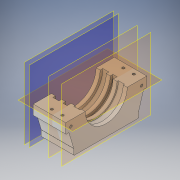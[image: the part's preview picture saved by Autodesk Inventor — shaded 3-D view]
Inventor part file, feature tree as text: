
AUTODESK INVENTOR PART (.ipt)
format: ipt  version: 2019 (Build 230136000, 136)  size: 584,192 bytes
history: native  units: mm
features: sketch x27, extrude x22, mirror x13, projected_geometry x13, plane x12, other x4, fillet x4, hole x3
ambient origin geometry x8: Origin, YZ Plane, XZ Plane, XY Plane, X Axis, Y Axis, Z Axis, Center Point
bodies: Body1 (feature_tree)
feature tree (98):
  other  "實體1"
  extrude  "擠出1"  Depth=123.43mm
  plane  "工作平面2"
  extrude  "擠出3"  Depth=160.0mm
  plane  "工作平面3"
  extrude  "擠出4"  Depth=120.0mm TaperAngle=0.0deg
  extrude  "擠出5"  [1 undecoded]
  plane  "工作平面4"
  extrude  "擠出7"  Depth=130.0mm
  plane  "工作平面5"
  extrude  "擠出9"  Depth=15.0mm TaperAngle=0.0deg
  extrude  "擠出10"  [1 undecoded]
  extrude  "擠出11"  Depth=111.375mm
  extrude  "擠出12"  Depth=10.0mm TaperAngle=0.0deg
  mirror  "鏡射1"
  fillet  "圓角2"  Radius=10.0mm
  fillet  "圓角3"  Radius=10.0mm
  sketch  "草圖16"
  plane  "工作平面7"
  mirror  "鏡射2"
  fillet  "圓角5"  [1 undecoded]
  fillet  "圓角6"  Radius=10.0mm
  plane  "工作平面8"
  plane  "工作平面9"
  sketch  "草圖20"
  extrude  "擠出15"  [1 undecoded]
  plane  "工作平面10"
  extrude  "擠出16"  Depth=10.0mm
  extrude  "擠出17"  Depth=10.0mm TaperAngle=0.0deg
  plane  "工作平面11"
  extrude  "擠出19"  Depth=10.0mm TaperAngle=0.0deg
  extrude  "擠出20"  Depth=160.0mm
  mirror  "鏡射3"
  mirror  "鏡射4"
  extrude  "擠出21"  Depth=80.0mm
  mirror  "鏡射7"
  plane  "工作平面15"
  mirror  "鏡射9"
  hole  "孔2"  [1 undecoded]
  mirror  "鏡射10"
  mirror  "鏡射11"
  hole  "孔3"  [1 undecoded]
  mirror  "鏡射12"
  mirror  "鏡射13"
  extrude  "擠出22"  Depth=160.0mm
  extrude  "擠出23"  Depth=120.0mm TaperAngle=0.0deg
  extrude  "擠出24"  Depth=120.0mm TaperAngle=0.0deg
  extrude  "擠出25"  Depth=25.0mm
  extrude  "擠出27"  Depth=20.0mm
  extrude  "擠出28"  Depth=2.0mm
  mirror  "鏡射14"
  plane  "工作平面17"
  hole  "孔4"  [1 undecoded]
  mirror  "鏡射15"
  mirror  "鏡射16"
  other  "分割2"
  other  "分割3"
  other  "分割4"
  extrude  "擠出29"  Depth=40.0mm
  sketch  "草圖1"
  sketch  "草圖4"
  sketch  "草圖6"
  sketch  "草圖7"
  projected_geometry  "投影迴路1"
  sketch  "草圖9"
  projected_geometry  "投影迴路4"
  sketch  "草圖11"
  sketch  "草圖12"
  projected_geometry  "投影迴路6"
  sketch  "草圖13"
  projected_geometry  "投影迴路7"
  sketch  "草圖14"
  plane  "工作平面6"
  sketch  "草圖17"
  projected_geometry  "投影迴路8"
  sketch  "草圖24"
  projected_geometry  "投影迴路11"
  sketch  "草圖25"
  sketch  "草圖26"
  sketch  "草圖27"
  sketch  "草圖28"
  sketch  "草圖29"
  projected_geometry  "投影迴路12"
  sketch  "草圖30"
  sketch  "草圖31"
  sketch  "草圖32"
  projected_geometry  "投影迴路13"
  projected_geometry  "投影迴路14"
  projected_geometry  "投影迴路15"
  sketch  "草圖33"
  sketch  "草圖34"
  sketch  "草圖35"
  projected_geometry  "投影迴路16"
  sketch  "草圖36"
  sketch  "草圖37"
  sketch  "草圖38"
  projected_geometry  "投影迴路17"
  projected_geometry  "投影迴路18"
note: 7 required parameter values undecoded (feature->parameter linkage not recoverable at this tier; creation-order binding heuristic only, values carry confidence <= 0.55)
